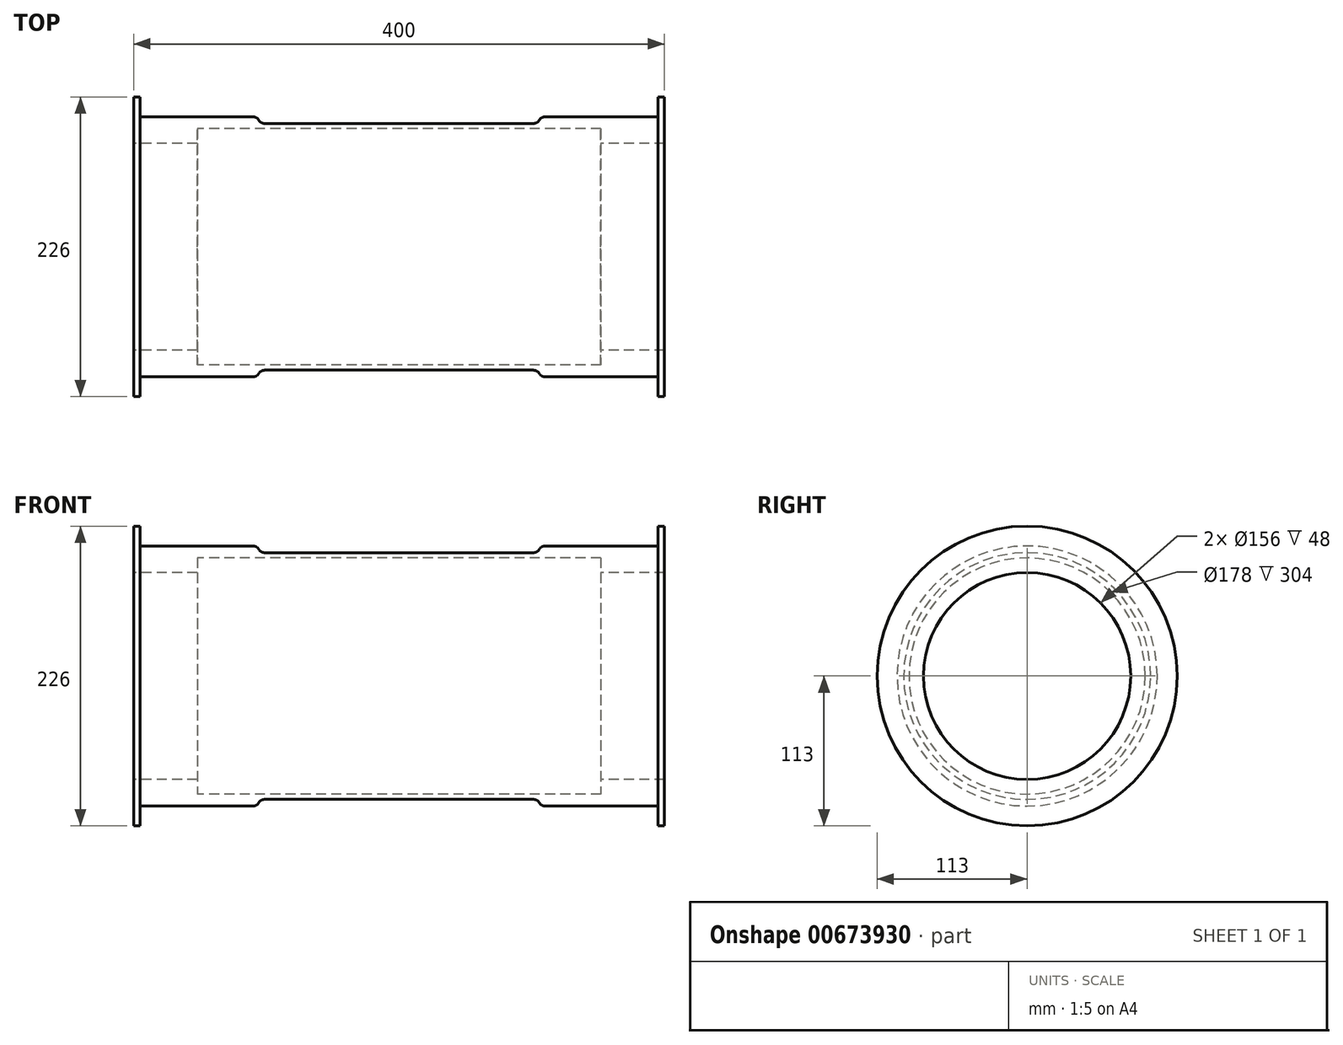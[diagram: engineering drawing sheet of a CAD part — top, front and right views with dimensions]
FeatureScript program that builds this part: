
annotation { "Feature Type Name" : "Feature", "Feature Type Description" : "" }
export const myFeature = defineFeature(function(context is Context, id is Id, definition is map)
    precondition{}
    {
        {
            var Q0;
            Q0=qCreatedBy(makeId("Top.planeOp"),FACE);
            var sketch = newSketch(context, id + "F0", { "sketchPlane" : qUnion([Q0])});
            skLineSegment(sketch, "E0.top", {"start": v(-110, 98) * mm, "end": v(-195, 98) * mm});
            skLineSegment(sketch, "E0.right", {"start": v(-200, 78) * mm, "end": v(-200, 98) * mm});
            skPoint(sketch, "E0.middle", {"position": v(0, 0) * mm});
            skLineSegment(sketch, "E1.top", {"start": v(0, 89) * mm, "end": v(-152, 89) * mm});
            skLineSegment(sketch, "E1.right", {"start": v(-152, 78) * mm, "end": v(-152, 89) * mm});
            skLineSegment(sketch, "E2", {"start": v(-200, 98) * mm, "end": v(-200, 113) * mm});
            skLineSegment(sketch, "E3", {"start": v(-200, 113) * mm, "end": v(-195, 113) * mm});
            skLineSegment(sketch, "E4", {"start": v(-195, 113) * mm, "end": v(-195, 98) * mm});
            skLineSegment(sketch, "E5", {"start": v(-195, 98) * mm, "end": v(-110, 98) * mm});
            skLineSegment(sketch, "E6", {"start": v(-200, 98) * mm, "end": v(-200, 78) * mm});
            skLineSegment(sketch, "E7", {"start": v(-200, 78) * mm, "end": v(-152, 78) * mm});
            skLineSegment(sketch, "E8", {"start": v(-105, 93) * mm, "end": v(-105, 93) * mm});
            skLineSegment(sketch, "E9", {"start": v(-101.34, 93) * mm, "end": v(0, 93) * mm});
            skLineSegment(sketch, "E10", {"start": v(0, 93) * mm, "end": v(0, 89) * mm});
            skPoint(sketch, "E1.bottom.end.orphan", {"position": v(-152, -89) * mm});
            skPoint(sketch, "E0.bottom.end.orphan", {"position": v(-200, -98) * mm});
            skPoint(sketch, "E1.left.start.orphan", {"position": v(152, -89) * mm});
            skPoint(sketch, "E0.left.end.orphan", {"position": v(200, 98) * mm});
            skPoint(sketch, "E0.left.start.orphan", {"position": v(200, -98) * mm});
            skPoint(sketch, "E11.orphan", {"position": v(152, 89) * mm});
            skPoint(sketch, "E12.visualSharp", {"position": v(-105, 98) * mm});
            skArc(sketch, "E12.filletArc", {"start": v(-105.67, 95.5) * mm, "mid": v(-107.5, 97.33) * mm, "end": v(-110, 98) * mm});
            skPoint(sketch, "E13.visualSharp", {"position": v(-105, 93) * mm});
            skArc(sketch, "E13.filletArc", {"start": v(-105.67, 95.5) * mm, "mid": v(-103.84, 93.67) * mm, "end": v(-101.34, 93) * mm});
            skArc(sketch, "E14.MirrorCS", {"start": v(105.67, 95.5) * mm, "mid": v(107.5, 97.33) * mm, "end": v(110, 98) * mm});
            skArc(sketch, "E15.MirrorCS", {"start": v(105.67, 95.5) * mm, "mid": v(103.84, 93.67) * mm, "end": v(101.34, 93) * mm});
            skLineSegment(sketch, "E16.MirrorCS", {"start": v(200, 78) * mm, "end": v(200, 98) * mm});
            skLineSegment(sketch, "E17.MirrorCS", {"start": v(200, 98) * mm, "end": v(200, 78) * mm});
            skLineSegment(sketch, "E18.MirrorCS", {"start": v(200, 98) * mm, "end": v(200, 113) * mm});
            skLineSegment(sketch, "E19.MirrorCS", {"start": v(195, 113) * mm, "end": v(195, 98) * mm});
            skLineSegment(sketch, "E20.MirrorCS", {"start": v(200, 113) * mm, "end": v(195, 113) * mm});
            skLineSegment(sketch, "E21.MirrorCS", {"start": v(152, 78) * mm, "end": v(152, 89) * mm});
            skLineSegment(sketch, "E22.MirrorCS", {"start": v(110, 98) * mm, "end": v(195, 98) * mm});
            skPoint(sketch, "E23.MirrorP", {"position": v(105, 93) * mm});
            skLineSegment(sketch, "E24.MirrorCS", {"start": v(195, 98) * mm, "end": v(110, 98) * mm});
            skPoint(sketch, "E25.MirrorP", {"position": v(105, 98) * mm});
            skLineSegment(sketch, "E26.MirrorCS", {"start": v(0, 89) * mm, "end": v(152, 89) * mm});
            skLineSegment(sketch, "E27.MirrorCS", {"start": v(200, 78) * mm, "end": v(152, 78) * mm});
            skLineSegment(sketch, "E28.MirrorCS", {"start": v(101.34, 93) * mm, "end": v(0, 93) * mm});
            skLineSegment(sketch, "E29.MirrorCS", {"start": v(105, 93) * mm, "end": v(105, 93) * mm});
            skLineSegment(sketch, "E30", {"start": v(-176.55, 0) * mm, "end": v(164.34, 0) * mm});
            skSolve(sketch);
        }
        {
            var Q0;
            Q0=makeQuery(id+"F0.imprint","IMPRINT",FACE,{"disambiguationData":[TD([[makeQuery(id+"F0.imprint","IMPRINT",EDGE,{"derivedFrom":sQuery(id+"F0.wireOp",EDGE,"E1.top")}),-1.0]])]});
            var Q1;
            Q1=makeQuery(id+"F0.imprint","IMPRINT",FACE,{"disambiguationData":[TD([[makeQuery(id+"F0.imprint","IMPRINT",EDGE,{"derivedFrom":sQuery(id+"F0.wireOp",EDGE,"E10")}),1.0]])]});
            var Q2;
            Q2=sQuery(id+"F0.wireOp",EDGE,"E30");
            revolve(context, id + "F1", {"entities" : qUnion([Q0, Q1]), "axis" : qUnion([Q2]), "revolveType" : RevolveType.FULL});
        }
    });
